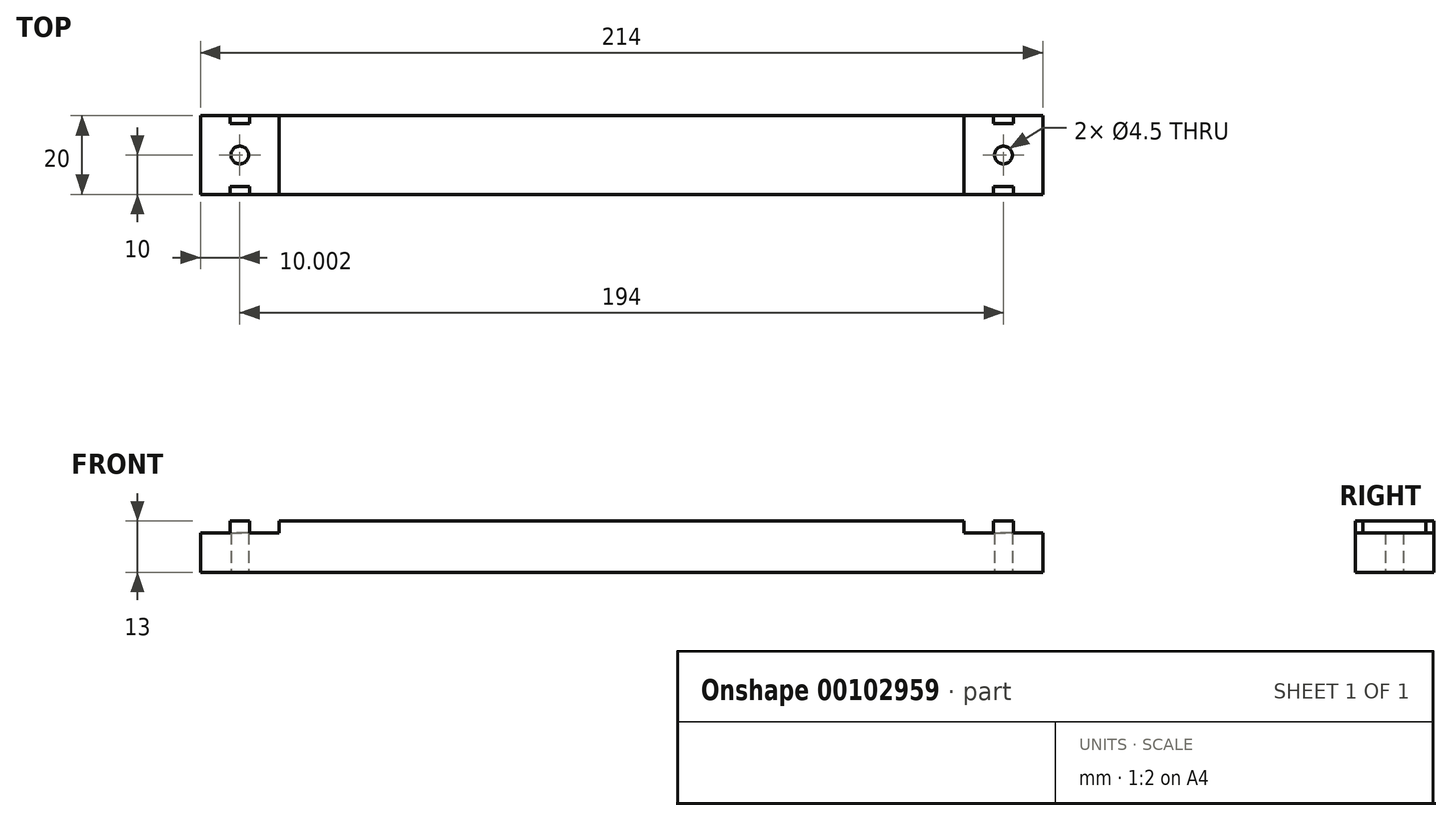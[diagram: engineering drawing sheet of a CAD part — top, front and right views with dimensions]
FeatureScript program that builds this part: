
annotation { "Feature Type Name" : "Feature", "Feature Type Description" : "" }
export const myFeature = defineFeature(function(context is Context, id is Id, definition is map)
    precondition{}
    {
        {
            var Q0;
            Q0=qCreatedBy(makeId("Top.planeOp"),FACE);
            var sketch = newSketch(context, id + "F0", { "sketchPlane" : qUnion([Q0])});
            skLineSegment(sketch, "E0.bottom", {"start": v(-45.86, 0) * mm, "end": v(168.14, 0) * mm});
            skLineSegment(sketch, "E0.top", {"start": v(-45.86, 20) * mm, "end": v(168.14, 20) * mm});
            skLineSegment(sketch, "E0.left", {"start": v(-45.86, 0) * mm, "end": v(-45.86, 20) * mm});
            skLineSegment(sketch, "E0.right", {"start": v(168.14, 0) * mm, "end": v(168.14, 20) * mm});
            skCircle(sketch, "E1", {"center": v(-35.86, 10) * mm, "radius": 2.25 * mm});
            skPoint(sketch, "E1.centerSnap0", {"position": v(-45.86, 10) * mm});
            skCircle(sketch, "E2", {"center": v(158.14, 10) * mm, "radius": 2.25 * mm});
            skPoint(sketch, "E2.centerSnap0", {"position": v(168.14, 10) * mm});
            skLineSegment(sketch, "E3", {"start": v(-25.86, 20) * mm, "end": v(-25.86, 0) * mm});
            skLineSegment(sketch, "E4", {"start": v(148.14, 0) * mm, "end": v(148.14, 20) * mm});
            skLineSegment(sketch, "E5.bottom", {"start": v(-38.36, 20) * mm, "end": v(-33.36, 20) * mm});
            skLineSegment(sketch, "E5.top", {"start": v(-38.36, 18) * mm, "end": v(-33.36, 18) * mm});
            skLineSegment(sketch, "E5.left", {"start": v(-38.36, 20) * mm, "end": v(-38.36, 18) * mm});
            skLineSegment(sketch, "E5.right", {"start": v(-33.36, 20) * mm, "end": v(-33.36, 18) * mm});
            skLineSegment(sketch, "E6.bottom", {"start": v(-38.36, 0) * mm, "end": v(-33.36, 0) * mm});
            skLineSegment(sketch, "E6.top", {"start": v(-38.36, 2) * mm, "end": v(-33.36, 2) * mm});
            skLineSegment(sketch, "E6.left", {"start": v(-38.36, 0) * mm, "end": v(-38.36, 2) * mm});
            skLineSegment(sketch, "E6.right", {"start": v(-33.36, 0) * mm, "end": v(-33.36, 2) * mm});
            skLineSegment(sketch, "E7.bottom", {"start": v(155.64, 20) * mm, "end": v(160.64, 20) * mm});
            skLineSegment(sketch, "E7.top", {"start": v(155.64, 18) * mm, "end": v(160.64, 18) * mm});
            skLineSegment(sketch, "E7.left", {"start": v(155.64, 20) * mm, "end": v(155.64, 18) * mm});
            skLineSegment(sketch, "E7.right", {"start": v(160.64, 20) * mm, "end": v(160.64, 18) * mm});
            skLineSegment(sketch, "E8.bottom", {"start": v(155.64, 0) * mm, "end": v(160.64, 0) * mm});
            skLineSegment(sketch, "E8.top", {"start": v(155.64, 2) * mm, "end": v(160.64, 2) * mm});
            skLineSegment(sketch, "E8.left", {"start": v(155.64, 0) * mm, "end": v(155.64, 2) * mm});
            skLineSegment(sketch, "E8.right", {"start": v(160.64, 0) * mm, "end": v(160.64, 2) * mm});
            skPoint(sketch, "E9", {"position": v(-35.86, 18) * mm});
            skPoint(sketch, "E10", {"position": v(158.14, 18) * mm});
            skSolve(sketch);
        }
        {
            var Q0;
            {var subQ0=sQuery(id+"F0.wireOp",EDGE,"E3");Q0=makeQuery(id+"F0.imprint","IMPRINT",FACE,{"disambiguationData":[TD([[makeQuery(id+"F0.imprint","IMPRINT",EDGE,{"derivedFrom":subQ0}),1.0]])]});}
            extrude(context, id + "F1", {"entities" : qUnion([Q0]), "depth" : 13 * mm});
        }
        {
            var Q0;
            {var subQ2=sQuery(id+"F0.wireOp",EDGE,"E0.left");Q0=makeQuery(id+"F0.imprint","IMPRINT",FACE,{"disambiguationData":[TD([[makeQuery(id+"F0.imprint","IMPRINT",EDGE,{"derivedFrom":subQ2}),-1.0]])]});}
            var Q1;
            {var subQ5=sQuery(id+"F0.wireOp",EDGE,"E0.right");Q1=makeQuery(id+"F0.imprint","IMPRINT",FACE,{"disambiguationData":[TD([[makeQuery(id+"F0.imprint","IMPRINT",EDGE,{"derivedFrom":subQ5}),1.0]])]});}
            extrude(context, id + "F2", {"entities" : qUnion([Q0, Q1]), "operationType" : NewBodyOperationType.ADD, "depth" : 10 * mm});
        }
        {
            var Q0;
            Q0=makeQuery(id+"F0.imprint","IMPRINT",FACE,{"disambiguationData":[TD([[makeQuery(id+"F0.imprint","IMPRINT",EDGE,{"derivedFrom":sQuery(id+"F0.wireOp",EDGE,"E5.top")}),1.0]])]});
            var Q1;
            Q1=makeQuery(id+"F0.imprint","IMPRINT",FACE,{"disambiguationData":[TD([[makeQuery(id+"F0.imprint","IMPRINT",EDGE,{"derivedFrom":sQuery(id+"F0.wireOp",EDGE,"E6.top")}),-1.0]])]});
            var Q2;
            Q2=makeQuery(id+"F0.imprint","IMPRINT",FACE,{"disambiguationData":[TD([[makeQuery(id+"F0.imprint","IMPRINT",EDGE,{"derivedFrom":sQuery(id+"F0.wireOp",EDGE,"E7.top")}),1.0]])]});
            var Q3;
            Q3=makeQuery(id+"F0.imprint","IMPRINT",FACE,{"disambiguationData":[TD([[makeQuery(id+"F0.imprint","IMPRINT",EDGE,{"derivedFrom":sQuery(id+"F0.wireOp",EDGE,"E8.top")}),-1.0]])]});
            extrude(context, id + "F3", {"entities" : qUnion([Q0, Q1, Q2, Q3]), "operationType" : NewBodyOperationType.ADD, "depth" : 13 * mm});
        }
    });
